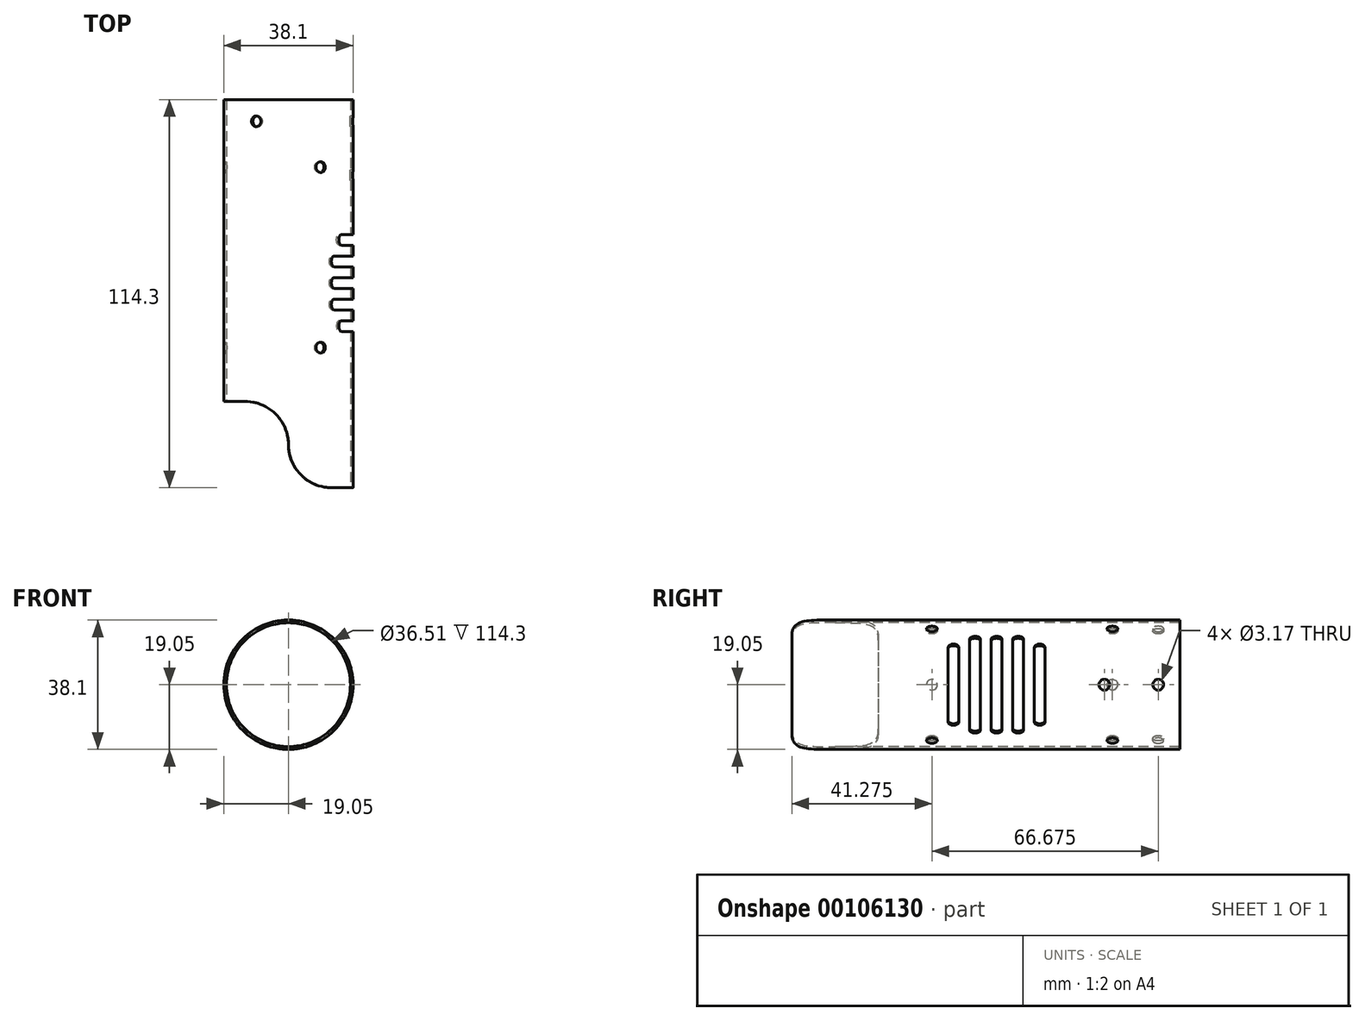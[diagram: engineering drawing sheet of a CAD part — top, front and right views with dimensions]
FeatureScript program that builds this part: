
annotation { "Feature Type Name" : "Feature", "Feature Type Description" : "" }
export const myFeature = defineFeature(function(context is Context, id is Id, definition is map)
    precondition{}
    {
        {
            var Q0;
            Q0=qCreatedBy(makeId("Right.planeOp"),FACE);
            var sketch = newSketch(context, id + "F0", { "sketchPlane" : qUnion([Q0])});
            skLineSegment(sketch, "E0", {"start": v(-152.4, 0) * mm, "end": v(152.4, 0) * mm, "construction": true});
            skLineSegment(sketch, "E1.bottom", {"start": v(-152.4, 19.05) * mm, "end": v(-38.1, 19.05) * mm});
            skLineSegment(sketch, "E1.top", {"start": v(-152.4, 18.26) * mm, "end": v(-38.1, 18.26) * mm});
            skLineSegment(sketch, "E1.left", {"start": v(-152.4, 19.05) * mm, "end": v(-152.4, 18.26) * mm});
            skLineSegment(sketch, "E1.right", {"start": v(-38.1, 19.05) * mm, "end": v(-38.1, 18.26) * mm});
            skSolve(sketch);
        }
        {
            var Q0;
            Q0 = qSketchRegion(id + "F0", true);
            var Q1;
            Q1=sQuery(id+"F0.wireOp",EDGE,"E0");
            revolve(context, id + "F1", {"entities" : qUnion([Q0]), "axis" : qUnion([Q1]), "revolveType" : RevolveType.FULL});
        }
        {
            var Q0;
            Q0=qCreatedBy(makeId("Top.planeOp"),FACE);
            var sketch = newSketch(context, id + "F2", { "sketchPlane" : qUnion([Q0])});
            skLineSegment(sketch, "E2", {"start": v(0, 0) * mm, "end": v(0, -152.4) * mm, "construction": true});
            skLineSegment(sketch, "E3", {"start": v(-12.7, -139.7) * mm, "end": v(12.7, -139.7) * mm, "construction": true});
            skArc(sketch, "E4", {"start": v(0, -139.7) * mm, "mid": v(-3.72, -130.72) * mm, "end": v(-12.7, -127) * mm});
            skArc(sketch, "E5", {"start": v(0, -139.7) * mm, "mid": v(3.72, -148.68) * mm, "end": v(12.7, -152.4) * mm});
            skLineSegment(sketch, "E6", {"start": v(12.7, -152.4) * mm, "end": v(-19.05, -152.4) * mm});
            skLineSegment(sketch, "E7", {"start": v(-19.05, -152.4) * mm, "end": v(-19.05, -127) * mm});
            skLineSegment(sketch, "E8", {"start": v(-19.05, -127) * mm, "end": v(-12.7, -127) * mm});
            skSolve(sketch);
        }
        {
            var Q0;
            Q0 = qSketchRegion(id + "F2", true);
            extrude(context, id + "F3", {"entities" : qUnion([Q0]), "operationType" : NewBodyOperationType.REMOVE, "oppositeDirection" : true, "depth" : 19.05 * mm, "hasSecondDirection" : true, "secondDirectionOppositeDirection" : false, "secondDirectionDepth" : 19.05 * mm});
        }
        {
            var Q0;
            Q0=qCreatedBy(makeId("Right.planeOp"),FACE);
            cPlane(context, id + "F4", {"entities" : qUnion([Q0]), "cplaneType" : CPlaneType.OFFSET, "offset" : 19.05 * mm, "width" : 152.4 * mm, "height" : 152.4 * mm});
        }
        {
            var Q0;
            Q0=qCreatedBy(id+"F4.planeOp",FACE);
            var sketch = newSketch(context, id + "F5", { "sketchPlane" : qUnion([Q0])});
            skLineSegment(sketch, "E9", {"start": v(0, 0) * mm, "end": v(-152.4, 0) * mm, "construction": true});
            skLineSegment(sketch, "E10", {"start": v(-92.08, 19.05) * mm, "end": v(-92.08, -19.05) * mm, "construction": true});
            skPoint(sketch, "E11", {"position": v(-92.08, 0) * mm});
            skArc(sketch, "E12", {"start": v(-90.49, 19.05) * mm, "mid": v(-92.08, 20.64) * mm, "end": v(-93.66, 19.05) * mm});
            skLineSegment(sketch, "E13", {"start": v(-85.72, 19.05) * mm, "end": v(-85.72, -19.05) * mm, "construction": true});
            skLineSegment(sketch, "E14", {"start": v(-98.43, 19.05) * mm, "end": v(-98.43, -19.05) * mm, "construction": true});
            skLineSegment(sketch, "E15", {"start": v(-104.78, 13.34) * mm, "end": v(-104.78, -13.34) * mm, "construction": true});
            skPoint(sketch, "E16", {"position": v(-98.43, 0) * mm});
            skPoint(sketch, "E17", {"position": v(-104.78, 0) * mm});
            skPoint(sketch, "E18", {"position": v(-85.72, 0) * mm});
            skPoint(sketch, "E19", {"position": v(-79.38, 0) * mm});
            skLineSegment(sketch, "E20", {"start": v(-79.38, 13.34) * mm, "end": v(-79.38, -13.34) * mm, "construction": true});
            skArc(sketch, "E21", {"start": v(-96.84, 19.05) * mm, "mid": v(-98.43, 20.64) * mm, "end": v(-100.01, 19.05) * mm});
            skArc(sketch, "E22", {"start": v(-84.14, 19.05) * mm, "mid": v(-85.72, 20.64) * mm, "end": v(-87.31, 19.05) * mm});
            skArc(sketch, "E23", {"start": v(-77.79, 13.34) * mm, "mid": v(-79.38, 14.92) * mm, "end": v(-80.96, 13.34) * mm});
            skArc(sketch, "E24", {"start": v(-103.19, 13.34) * mm, "mid": v(-104.78, 14.92) * mm, "end": v(-106.36, 13.34) * mm});
            skArc(sketch, "E25.MirrorC", {"start": v(-77.79, -13.34) * mm, "mid": v(-79.38, -14.92) * mm, "end": v(-80.96, -13.34) * mm});
            skArc(sketch, "E26.MirrorC", {"start": v(-84.14, -19.05) * mm, "mid": v(-85.72, -20.64) * mm, "end": v(-87.31, -19.05) * mm});
            skArc(sketch, "E27.MirrorC", {"start": v(-96.84, -19.05) * mm, "mid": v(-98.43, -20.64) * mm, "end": v(-100.01, -19.05) * mm});
            skArc(sketch, "E28.MirrorC", {"start": v(-90.49, -19.05) * mm, "mid": v(-92.08, -20.64) * mm, "end": v(-93.66, -19.05) * mm});
            skArc(sketch, "E29.MirrorC", {"start": v(-103.19, -13.34) * mm, "mid": v(-104.78, -14.92) * mm, "end": v(-106.36, -13.34) * mm});
            skLineSegment(sketch, "E30", {"start": v(-106.36, 13.34) * mm, "end": v(-106.36, -13.34) * mm});
            skLineSegment(sketch, "E31", {"start": v(-103.19, 13.34) * mm, "end": v(-103.19, -13.34) * mm});
            skLineSegment(sketch, "E32", {"start": v(-100.01, 19.05) * mm, "end": v(-100.01, -19.05) * mm});
            skLineSegment(sketch, "E33", {"start": v(-96.84, 19.05) * mm, "end": v(-96.84, -19.05) * mm});
            skLineSegment(sketch, "E34", {"start": v(-93.66, 19.05) * mm, "end": v(-93.66, -19.05) * mm});
            skLineSegment(sketch, "E35", {"start": v(-90.49, 19.05) * mm, "end": v(-90.49, -19.05) * mm});
            skLineSegment(sketch, "E36", {"start": v(-87.31, 19.05) * mm, "end": v(-87.31, -19.05) * mm});
            skLineSegment(sketch, "E37", {"start": v(-84.14, 19.05) * mm, "end": v(-84.14, -19.05) * mm});
            skLineSegment(sketch, "E38", {"start": v(-80.96, 13.34) * mm, "end": v(-80.96, -13.34) * mm});
            skLineSegment(sketch, "E39", {"start": v(-77.79, 13.34) * mm, "end": v(-77.79, -13.34) * mm});
            skSolve(sketch);
        }
        {
            var Q0;
            Q0=qCreatedBy(makeId("Right.planeOp"),FACE);
            cPlane(context, id + "F6", {"entities" : qUnion([Q0]), "cplaneType" : CPlaneType.OFFSET, "offset" : 6.35 * mm, "width" : 152.4 * mm, "height" : 152.4 * mm});
        }
        {
            var Q0;
            Q0=qCreatedBy(id+"F6.planeOp",FACE);
            var sketch = newSketch(context, id + "F7", { "sketchPlane" : qUnion([Q0])});
            skLineSegment(sketch, "E40", {"start": v(0, 0) * mm, "end": v(-152.4, 0) * mm, "construction": true});
            skPoint(sketch, "E41", {"position": v(-104.78, 0) * mm});
            skPoint(sketch, "E42", {"position": v(-98.43, 0) * mm});
            skPoint(sketch, "E43", {"position": v(-92.08, 0) * mm});
            skPoint(sketch, "E44", {"position": v(-85.72, 0) * mm});
            skPoint(sketch, "E45", {"position": v(-79.38, 0) * mm});
            skLineSegment(sketch, "E46", {"start": v(-104.78, 4.45) * mm, "end": v(-104.78, -4.45) * mm, "construction": true});
            skLineSegment(sketch, "E47", {"start": v(-92.08, 6.35) * mm, "end": v(-92.08, -6.35) * mm, "construction": true});
            skLineSegment(sketch, "E48", {"start": v(-79.38, 4.45) * mm, "end": v(-79.38, -4.45) * mm, "construction": true});
            skLineSegment(sketch, "E49", {"start": v(-98.43, 6.35) * mm, "end": v(-98.43, -6.35) * mm, "construction": true});
            skLineSegment(sketch, "E50", {"start": v(-85.72, 6.35) * mm, "end": v(-85.72, -6.35) * mm, "construction": true});
            skArc(sketch, "E51", {"start": v(-103.19, 4.45) * mm, "mid": v(-104.78, 6.03) * mm, "end": v(-106.36, 4.45) * mm});
            skArc(sketch, "E52", {"start": v(-96.84, 6.35) * mm, "mid": v(-98.43, 7.94) * mm, "end": v(-100.01, 6.35) * mm});
            skArc(sketch, "E53", {"start": v(-90.49, 6.35) * mm, "mid": v(-92.08, 7.94) * mm, "end": v(-93.66, 6.35) * mm});
            skArc(sketch, "E54", {"start": v(-84.14, 6.35) * mm, "mid": v(-85.72, 7.94) * mm, "end": v(-87.31, 6.35) * mm});
            skArc(sketch, "E55", {"start": v(-77.79, 4.45) * mm, "mid": v(-79.38, 6.03) * mm, "end": v(-80.96, 4.45) * mm});
            skArc(sketch, "E56.MirrorC", {"start": v(-90.49, -6.35) * mm, "mid": v(-92.08, -7.94) * mm, "end": v(-93.66, -6.35) * mm});
            skArc(sketch, "E57.MirrorC", {"start": v(-96.84, -6.35) * mm, "mid": v(-98.43, -7.94) * mm, "end": v(-100.01, -6.35) * mm});
            skArc(sketch, "E58.MirrorC", {"start": v(-84.14, -6.35) * mm, "mid": v(-85.72, -7.94) * mm, "end": v(-87.31, -6.35) * mm});
            skArc(sketch, "E59.MirrorC", {"start": v(-103.19, -4.45) * mm, "mid": v(-104.78, -6.03) * mm, "end": v(-106.36, -4.45) * mm});
            skArc(sketch, "E60.MirrorC", {"start": v(-77.79, -4.45) * mm, "mid": v(-79.38, -6.03) * mm, "end": v(-80.96, -4.45) * mm});
            skLineSegment(sketch, "E61", {"start": v(-106.36, 4.45) * mm, "end": v(-106.36, -4.45) * mm});
            skLineSegment(sketch, "E62", {"start": v(-103.19, 4.45) * mm, "end": v(-103.19, -4.45) * mm});
            skLineSegment(sketch, "E63", {"start": v(-100.01, 6.35) * mm, "end": v(-100.01, -6.35) * mm});
            skLineSegment(sketch, "E64", {"start": v(-96.84, 6.35) * mm, "end": v(-96.84, -6.35) * mm});
            skLineSegment(sketch, "E65", {"start": v(-93.66, 6.35) * mm, "end": v(-93.66, -6.35) * mm});
            skLineSegment(sketch, "E66", {"start": v(-90.49, 6.35) * mm, "end": v(-90.49, -6.35) * mm});
            skLineSegment(sketch, "E67", {"start": v(-87.31, 6.35) * mm, "end": v(-87.31, -6.35) * mm});
            skLineSegment(sketch, "E68", {"start": v(-84.14, 6.35) * mm, "end": v(-84.14, -6.35) * mm});
            skLineSegment(sketch, "E69", {"start": v(-80.96, 4.45) * mm, "end": v(-80.96, -4.45) * mm});
            skLineSegment(sketch, "E70", {"start": v(-77.79, 4.45) * mm, "end": v(-77.79, -4.45) * mm});
            skSolve(sketch);
        }
        {
            var Q0;
            Q0=makeQuery(id+"F5.imprint","IMPRINT",FACE,{"disambiguationData":[TD([[makeQuery(id+"F5.imprint","IMPRINT",EDGE,{"derivedFrom":sQuery(id+"F5.wireOp",EDGE,"E24")}),1.0]])]});
            var Q1;
            Q1=makeQuery(id+"F7.imprint","IMPRINT",FACE,{"disambiguationData":[TD([[makeQuery(id+"F7.imprint","IMPRINT",EDGE,{"derivedFrom":sQuery(id+"F7.wireOp",EDGE,"E51")}),1.0]])]});
            loft(context, id + "F8", {"operationType" : NewBodyOperationType.REMOVE, "sheetProfilesArray" : [{ "sheetProfileEntities" : qUnion([Q0]) }, { "sheetProfileEntities" : qUnion([Q1]) }]});
        }
        {
            var Q0;
            Q0=makeQuery(id+"F7.imprint","IMPRINT",FACE,{"disambiguationData":[TD([[makeQuery(id+"F7.imprint","IMPRINT",EDGE,{"derivedFrom":sQuery(id+"F7.wireOp",EDGE,"E52")}),1.0]])]});
            var Q1;
            Q1=makeQuery(id+"F5.imprint","IMPRINT",FACE,{"disambiguationData":[TD([[makeQuery(id+"F5.imprint","IMPRINT",EDGE,{"derivedFrom":sQuery(id+"F5.wireOp",EDGE,"E21")}),1.0]])]});
            loft(context, id + "F9", {"operationType" : NewBodyOperationType.REMOVE, "sheetProfilesArray" : [{ "sheetProfileEntities" : qUnion([Q0]) }, { "sheetProfileEntities" : qUnion([Q1]) }]});
        }
        {
            var Q1;
            Q1=makeQuery(id+"F7.imprint","IMPRINT",FACE,{"disambiguationData":[TD([[makeQuery(id+"F7.imprint","IMPRINT",EDGE,{"derivedFrom":sQuery(id+"F7.wireOp",EDGE,"E53")}),1.0]])]});
            var Q2;
            Q2=makeQuery(id+"F5.imprint","IMPRINT",FACE,{"disambiguationData":[TD([[makeQuery(id+"F5.imprint","IMPRINT",EDGE,{"derivedFrom":sQuery(id+"F5.wireOp",EDGE,"E12")}),1.0]])]});
            loft(context, id + "F10", {"operationType" : NewBodyOperationType.REMOVE, "sheetProfilesArray" : [{ "sheetProfileEntities" : qUnion([Q1]) }, { "sheetProfileEntities" : qUnion([Q2]) }]});
        }
        {
            var Q1;
            Q1=makeQuery(id+"F7.imprint","IMPRINT",FACE,{"disambiguationData":[TD([[makeQuery(id+"F7.imprint","IMPRINT",EDGE,{"derivedFrom":sQuery(id+"F7.wireOp",EDGE,"E54")}),1.0]])]});
            var Q2;
            Q2=makeQuery(id+"F5.imprint","IMPRINT",FACE,{"disambiguationData":[TD([[makeQuery(id+"F5.imprint","IMPRINT",EDGE,{"derivedFrom":sQuery(id+"F5.wireOp",EDGE,"E22")}),1.0]])]});
            loft(context, id + "F11", {"operationType" : NewBodyOperationType.REMOVE, "sheetProfilesArray" : [{ "sheetProfileEntities" : qUnion([Q1]) }, { "sheetProfileEntities" : qUnion([Q2]) }]});
        }
        {
            var Q0;
            Q0=makeQuery(id+"F7.imprint","IMPRINT",FACE,{"disambiguationData":[TD([[makeQuery(id+"F7.imprint","IMPRINT",EDGE,{"derivedFrom":sQuery(id+"F7.wireOp",EDGE,"E55")}),1.0]])]});
            var Q1;
            Q1=makeQuery(id+"F5.imprint","IMPRINT",FACE,{"disambiguationData":[TD([[makeQuery(id+"F5.imprint","IMPRINT",EDGE,{"derivedFrom":sQuery(id+"F5.wireOp",EDGE,"E23")}),1.0]])]});
            loft(context, id + "F12", {"operationType" : NewBodyOperationType.REMOVE, "sheetProfilesArray" : [{ "sheetProfileEntities" : qUnion([Q0]) }, { "sheetProfileEntities" : qUnion([Q1]) }]});
        }
        {
            var Q0;
            Q0=qCreatedBy(makeId("Right.planeOp"),FACE);
            var sketch = newSketch(context, id + "F13", { "sketchPlane" : qUnion([Q0])});
            skLineSegment(sketch, "E71", {"start": v(0, 0) * mm, "end": v(-152.4, 0) * mm, "construction": true});
            skCircle(sketch, "E72", {"center": v(-111.12, 0) * mm, "radius": 1.59 * mm});
            skCircle(sketch, "E73", {"center": v(-57.94, 0) * mm, "radius": 1.59 * mm});
            skSolve(sketch);
        }
        {
            var Q0;
            Q0 = qSketchRegion(id + "F13", true);
            var Q1;
            Q1=makeQuery(id+"F1.opRevolve","SWEPT_FACE",FACE,{"disambiguationData":[OSD([sQuery(id+"F0.wireOp",EDGE,"E1.bottom")])]});
            extrude(context, id + "F14", {"entities" : qUnion([Q0]), "operationType" : NewBodyOperationType.REMOVE, "endBound" : BoundingType.UP_TO_SURFACE, "oppositeDirection" : true, "endBoundEntityFace" : qUnion([Q1]), "depth" : 25.4 * mm});
        }
        {
            var Q0;
            Q0=qCreatedBy(makeId("Right.planeOp"),FACE);
            var sketch = newSketch(context, id + "F15", { "sketchPlane" : qUnion([Q0])});
            skLineSegment(sketch, "E74", {"start": v(0, 0) * mm, "end": v(-152.4, 0) * mm, "construction": true});
            skCircle(sketch, "E75", {"center": v(-60.33, 0) * mm, "radius": 1.59 * mm});
            skCircle(sketch, "E76", {"center": v(-44.45, 0) * mm, "radius": 1.59 * mm});
            skSolve(sketch);
        }
        {
            var Q0;
            Q0 = qSketchRegion(id + "F15", true);
            var Q1;
            Q1=makeQuery(id+"F1.opRevolve","SWEPT_FACE",FACE,{"disambiguationData":[OSD([sQuery(id+"F0.wireOp",EDGE,"E1.bottom")])]});
            extrude(context, id + "F16", {"entities" : qUnion([Q0]), "operationType" : NewBodyOperationType.REMOVE, "endBound" : BoundingType.UP_TO_SURFACE, "endBoundEntityFace" : qUnion([Q1]), "depth" : 25.4 * mm});
        }
        {
            var Q0;
            Q0=qCreatedBy(makeId("Front.planeOp"),FACE);
            var sketch = newSketch(context, id + "F17", { "sketchPlane" : qUnion([Q0])});
            skLineSegment(sketch, "E77", {"start": v(-19.05, 0) * mm, "end": v(19.05, 0) * mm, "construction": true});
            skLineSegment(sketch, "E78", {"start": v(0, 19.05) * mm, "end": v(0, -19.05) * mm, "construction": true});
            skLineSegment(sketch, "E79", {"start": v(-16.5, -9.53) * mm, "end": v(16.5, 9.53) * mm, "construction": true});
            skLineSegment(sketch, "E80.MirrorCS", {"start": v(16.5, -9.53) * mm, "end": v(-16.5, 9.53) * mm, "construction": true});
            skPoint(sketch, "E81", {"position": v(0, 0) * mm});
            skSolve(sketch);
        }
        {
            var Q0;
            Q0=sQuery(id+"F17.wireOp",VERTEX,"E80.MirrorCS.end");
            var Q1;
            Q1=sQuery(id+"F17.wireOp",VERTEX,"E80.MirrorCS.start");
            var Q2;
            Q2=sQuery(id+"F0.wireOp",VERTEX,"E0.start");
            cPlane(context, id + "F18", {"entities" : qUnion([Q0, Q1, Q2]), "cplaneType" : CPlaneType.THREE_POINT, "offset" : 25.4 * mm, "width" : 152.4 * mm, "height" : 152.4 * mm});
        }
        {
            var Q0;
            Q0=qCreatedBy(id+"F18.planeOp",FACE);
            var sketch = newSketch(context, id + "F19", { "sketchPlane" : qUnion([Q0])});
            skLineSegment(sketch, "E82", {"start": v(0, 0) * mm, "end": v(0, -152.4) * mm, "construction": true});
            skCircle(sketch, "E83", {"center": v(0, -111.12) * mm, "radius": 1.59 * mm});
            skCircle(sketch, "E84", {"center": v(0, -57.94) * mm, "radius": 1.59 * mm});
            skSolve(sketch);
        }
        {
            var Q0;
            Q0 = qSketchRegion(id + "F19", true);
            var Q1;
            Q1=makeQuery(id+"F1.opRevolve","SWEPT_FACE",FACE,{"disambiguationData":[OSD([sQuery(id+"F0.wireOp",EDGE,"E1.bottom")])]});
            extrude(context, id + "F20", {"entities" : qUnion([Q0]), "operationType" : NewBodyOperationType.REMOVE, "endBound" : BoundingType.UP_TO_SURFACE, "endBoundEntityFace" : qUnion([Q1]), "depth" : 25.4 * mm});
        }
        {
            var Q0;
            Q0=sQuery(id+"F17.wireOp",VERTEX,"E79.end");
            var Q1;
            Q1=sQuery(id+"F17.wireOp",VERTEX,"E79.start");
            var Q2;
            Q2=sQuery(id+"F0.wireOp",VERTEX,"E0.start");
            cPlane(context, id + "F21", {"entities" : qUnion([Q0, Q1, Q2]), "cplaneType" : CPlaneType.THREE_POINT, "offset" : 25.4 * mm, "width" : 152.4 * mm, "height" : 152.4 * mm});
        }
        {
            var Q0;
            Q0=qCreatedBy(id+"F21.planeOp",FACE);
            var sketch = newSketch(context, id + "F22", { "sketchPlane" : qUnion([Q0])});
            skLineSegment(sketch, "E85", {"start": v(0, 0) * mm, "end": v(0, 152.4) * mm, "construction": true});
            skCircle(sketch, "E86", {"center": v(0, 111.12) * mm, "radius": 1.59 * mm});
            skCircle(sketch, "E87", {"center": v(0, 57.94) * mm, "radius": 1.59 * mm});
            skSolve(sketch);
        }
        {
            var Q0;
            Q0 = qSketchRegion(id + "F22", true);
            var Q1;
            Q1=makeQuery(id+"F1.opRevolve","SWEPT_FACE",FACE,{"disambiguationData":[OSD([sQuery(id+"F0.wireOp",EDGE,"E1.bottom")])]});
            extrude(context, id + "F23", {"entities" : qUnion([Q0]), "operationType" : NewBodyOperationType.REMOVE, "endBound" : BoundingType.UP_TO_SURFACE, "endBoundEntityFace" : qUnion([Q1]), "depth" : 25.4 * mm});
        }
        {
            var Q0;
            Q0=qCreatedBy(id+"F18.planeOp",FACE);
            var sketch = newSketch(context, id + "F24", { "sketchPlane" : qUnion([Q0])});
            skCircle(sketch, "E88", {"center": v(0, -44.45) * mm, "radius": 1.59 * mm});
            skSolve(sketch);
        }
        {
            var Q0;
            Q0 = qSketchRegion(id + "F24", true);
            var Q1;
            Q1=makeQuery(id+"F1.opRevolve","SWEPT_FACE",FACE,{"disambiguationData":[OSD([sQuery(id+"F0.wireOp",EDGE,"E1.bottom")])]});
            extrude(context, id + "F25", {"entities" : qUnion([Q0]), "operationType" : NewBodyOperationType.REMOVE, "endBound" : BoundingType.UP_TO_SURFACE, "oppositeDirection" : true, "endBoundEntityFace" : qUnion([Q1]), "depth" : 25.4 * mm});
        }
        {
            var Q0;
            Q0=qCreatedBy(id+"F21.planeOp",FACE);
            var sketch = newSketch(context, id + "F26", { "sketchPlane" : qUnion([Q0])});
            skCircle(sketch, "E89", {"center": v(0, 44.45) * mm, "radius": 1.59 * mm});
            skSolve(sketch);
        }
        {
            var Q0;
            Q0 = qSketchRegion(id + "F26", true);
            var Q1;
            Q1=makeQuery(id+"F1.opRevolve","SWEPT_FACE",FACE,{"disambiguationData":[OSD([sQuery(id+"F0.wireOp",EDGE,"E1.bottom")])]});
            extrude(context, id + "F27", {"entities" : qUnion([Q0]), "operationType" : NewBodyOperationType.REMOVE, "endBound" : BoundingType.UP_TO_SURFACE, "oppositeDirection" : true, "endBoundEntityFace" : qUnion([Q1]), "depth" : 25.4 * mm});
        }
    });
